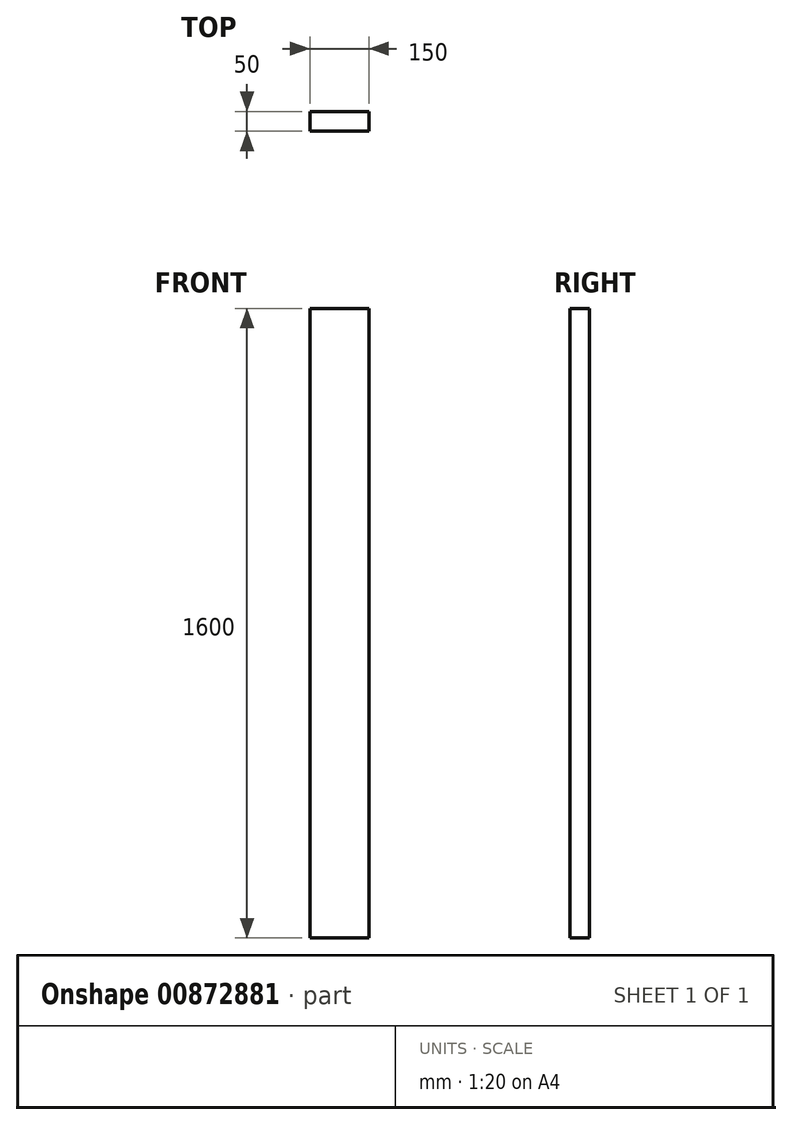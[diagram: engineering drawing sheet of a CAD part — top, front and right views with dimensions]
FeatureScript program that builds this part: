
annotation { "Feature Type Name" : "Feature", "Feature Type Description" : "" }
export const myFeature = defineFeature(function(context is Context, id is Id, definition is map)
    precondition{}
    {
        {
            var Q0;
            Q0=qCreatedBy(makeId("Top.planeOp"),FACE);
            var sketch = newSketch(context, id + "F0", { "sketchPlane" : qUnion([Q0])});
            skLineSegment(sketch, "E0.bottom", {"start": v(0, 0) * mm, "end": v(150, 0) * mm});
            skLineSegment(sketch, "E0.top", {"start": v(0, -50) * mm, "end": v(150, -50) * mm});
            skLineSegment(sketch, "E0.left", {"start": v(0, 0) * mm, "end": v(0, -50) * mm});
            skLineSegment(sketch, "E0.right", {"start": v(150, 0) * mm, "end": v(150, -50) * mm});
            skSolve(sketch);
        }
        {
            var Q0;
            Q0=makeQuery(id+"F0.imprint","IMPRINT",FACE,{"disambiguationData":[TD([[makeQuery(id+"F0.imprint","IMPRINT",EDGE,{"derivedFrom":sQuery(id+"F0.wireOp",EDGE,"E0.bottom")}),-1.0]])]});
            extrude(context, id + "F1", {"entities" : qUnion([Q0]), "depth" : 1600 * mm, "offsetDistance" : 25 * mm});
        }
    });
